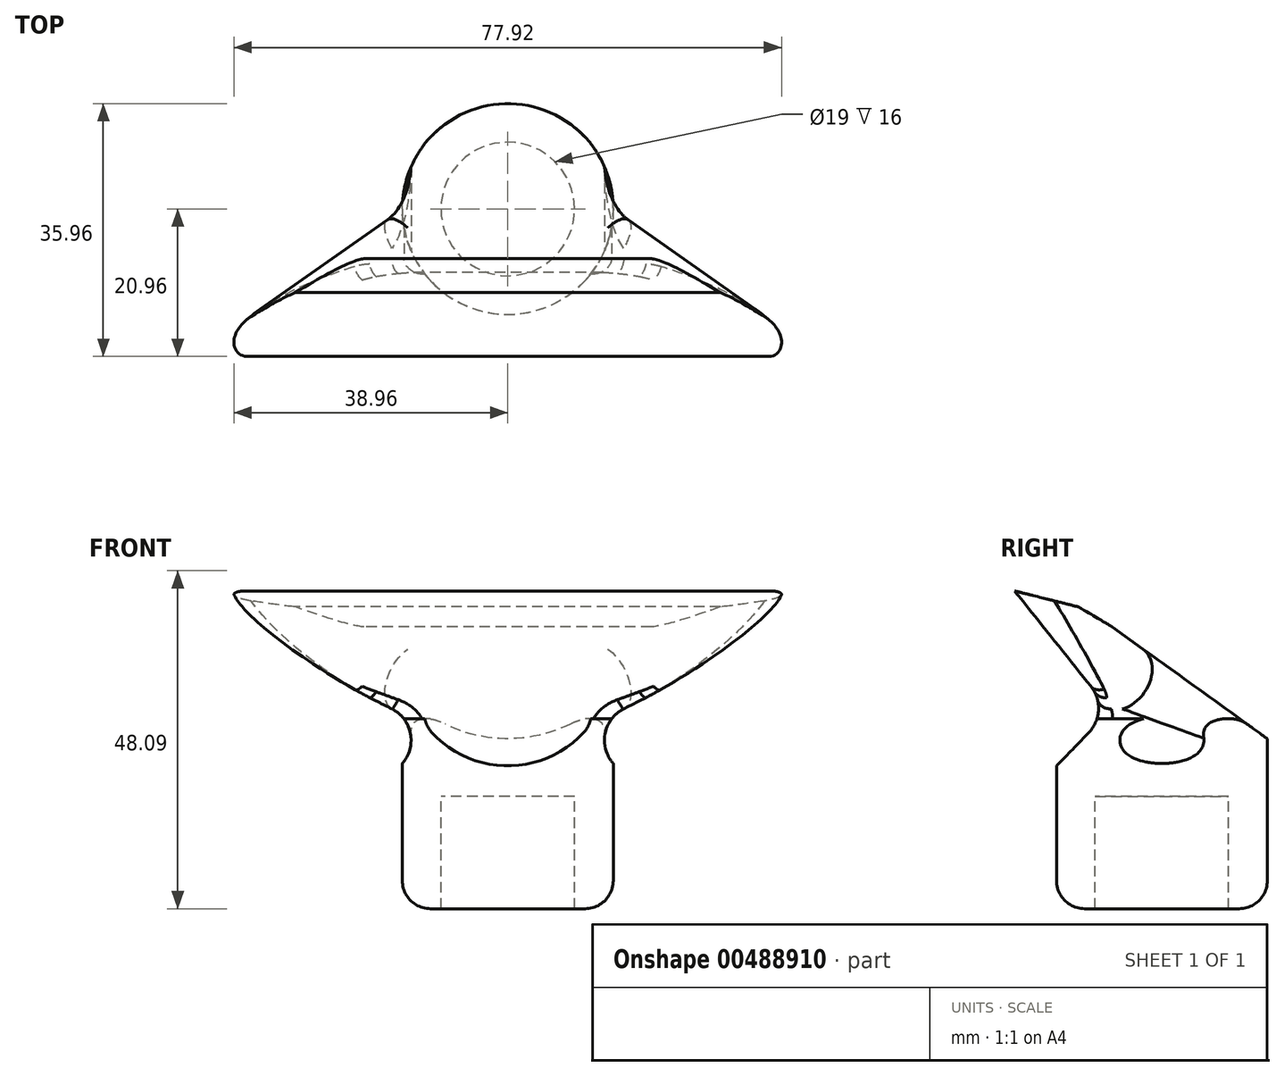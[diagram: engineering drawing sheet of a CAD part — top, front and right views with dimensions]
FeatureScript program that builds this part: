
annotation { "Feature Type Name" : "Feature", "Feature Type Description" : "" }
export const myFeature = defineFeature(function(context is Context, id is Id, definition is map)
    precondition{}
    {
        {
            var Q0;
            Q0=qCreatedBy(makeId("Top.planeOp"),FACE);
            var sketch = newSketch(context, id + "F0", { "sketchPlane" : qUnion([Q0])});
            skCircle(sketch, "E0", {"center": v(0, 0) * mm, "radius": 9.5 * mm});
            skCircle(sketch, "E1", {"center": v(0, 0) * mm, "radius": 15 * mm});
            skSolve(sketch);
        }
        {
            var Q0;
            Q0=makeQuery(id+"F0.imprint","IMPRINT",FACE,{"disambiguationData":[TD([[makeQuery(id+"F0.imprint","IMPRINT",EDGE,{"derivedFrom":sQuery(id+"F0.wireOp",EDGE,"E0")}),-1.0]])]});
            extrude(context, id + "F1", {"entities" : qUnion([Q0]), "oppositeDirection" : true, "depth" : 20 * mm, "offsetDistance" : 25 * mm});
        }
        {
            var Q0;
            Q0=makeQuery(id+"F1.opExtrude","CAP_EDGE",EDGE,{"disambiguationData":[OSD([sQuery(id+"F0.wireOp",EDGE,"E1")])],"isStart":false});
            fillet(context, id + "F2", {"entities" : qUnion([Q0]), "radius" : 4 * mm, "tangentPropagation" : true, "allowEdgeOverflow" : false});
        }
        {
            var Q0;
            Q0=makeQuery(id+"F0.imprint","IMPRINT",FACE,{"disambiguationData":[TD([[makeQuery(id+"F0.imprint","IMPRINT",EDGE,{"derivedFrom":sQuery(id+"F0.wireOp",EDGE,"E0")}),1.0]])]});
            extrude(context, id + "F3", {"entities" : qUnion([Q0]), "operationType" : NewBodyOperationType.ADD, "oppositeDirection" : true, "depth" : 4 * mm, "offsetDistance" : 25 * mm});
        }
        {
            var Q0;
            Q0=qCreatedBy(makeId("Right.planeOp"),FACE);
            var sketch = newSketch(context, id + "F4", { "sketchPlane" : qUnion([Q0])});
            skLineSegment(sketch, "E2", {"start": v(-7.08, 20.11) * mm, "end": v(15.3, 3.97) * mm});
            skLineSegment(sketch, "E3", {"start": v(15.3, 3.97) * mm, "end": v(15.3, 0) * mm});
            skLineSegment(sketch, "E4", {"start": v(15.3, 0) * mm, "end": v(-15.3, 0) * mm});
            skLineSegment(sketch, "E5", {"start": v(-15.3, 0) * mm, "end": v(-10.42, 5.05) * mm});
            skLineSegment(sketch, "E6", {"start": v(-10.11, 11.65) * mm, "end": v(-20.96, 25.21) * mm});
            skLineSegment(sketch, "E7", {"start": v(-20.96, 25.21) * mm, "end": v(-11.9, 22.95) * mm});
            skLineSegment(sketch, "E8", {"start": v(-11.9, 22.95) * mm, "end": v(-7.08, 20.11) * mm});
            skPoint(sketch, "E9.visualSharp", {"position": v(-7.37, 8.21) * mm});
            skArc(sketch, "E9.filletArc", {"start": v(-10.42, 5.05) * mm, "mid": v(-9.02, 8.3) * mm, "end": v(-10.11, 11.65) * mm});
            skSolve(sketch);
        }
        {
            var Q0;
            Q0=makeQuery(id+"F4.imprint","IMPRINT",FACE,{"disambiguationData":[TD([[makeQuery(id+"F4.imprint","IMPRINT",EDGE,{"derivedFrom":sQuery(id+"F4.wireOp",EDGE,"E2")}),-1.0]])]});
            extrude(context, id + "F5", {"entities" : qUnion([Q0]), "operationType" : NewBodyOperationType.ADD, "depth" : 40 * mm, "offsetDistance" : 25 * mm, "hasSecondDirection" : true, "secondDirectionOppositeDirection" : true, "secondDirectionDepth" : 40 * mm});
        }
        {
            var Q0;
            Q0=qCreatedBy(makeId("Front.planeOp"),FACE);
            var sketch = newSketch(context, id + "F6", { "sketchPlane" : qUnion([Q0])});
            skLineSegment(sketch, "E10", {"start": v(19.55, -5.1) * mm, "end": v(11.05, 5.67) * mm});
            skLineSegment(sketch, "E11", {"start": v(11.05, 5.67) * mm, "end": v(46.17, 23.51) * mm});
            skLineSegment(sketch, "E12", {"start": v(46.17, 23.51) * mm, "end": v(59.38, -2.48) * mm});
            skLineSegment(sketch, "E13", {"start": v(59.38, -2.48) * mm, "end": v(19.55, -5.1) * mm});
            skSolve(sketch);
        }
        {
            var Q0;
            Q0=makeQuery(id+"F6.imprint","IMPRINT",FACE,{"disambiguationData":[TD([[makeQuery(id+"F6.imprint","IMPRINT",EDGE,{"derivedFrom":sQuery(id+"F6.wireOp",EDGE,"E10")}),-1.0]])]});
            extrude(context, id + "F7", {"entities" : qUnion([Q0]), "depth" : 25 * mm, "offsetDistance" : 25 * mm, "hasSecondDirection" : true, "secondDirectionOppositeDirection" : true, "secondDirectionDepth" : 25 * mm});
        }
        {
            var Q0;
            Q0=makeQuery(id+"F7.opExtrude","SWEPT_BODY",BODY,{"disambiguationData":[OSD([sQuery(id+"F6.wireOp",EDGE,"E10"),sQuery(id+"F6.wireOp",EDGE,"E11"),sQuery(id+"F6.wireOp",EDGE,"E12"),sQuery(id+"F6.wireOp",EDGE,"E13")])]});
            var Q1;
            Q1=qCreatedBy(makeId("Right.planeOp"),FACE);
            mirror(context, id + "F8", {"entities" : qUnion([Q0]), "mirrorPlane" : qUnion([Q1])});
        }
        {
            var Q0;
            Q0=makeQuery(id+"F7.opExtrude","SWEPT_BODY",BODY,{"disambiguationData":[OSD([sQuery(id+"F6.wireOp",EDGE,"E10"),sQuery(id+"F6.wireOp",EDGE,"E11"),sQuery(id+"F6.wireOp",EDGE,"E12"),sQuery(id+"F6.wireOp",EDGE,"E13")])]});
            var Q1;
            Q1=makeQuery(id+"F8.opPattern","COPY",BODY,{"derivedFrom":makeQuery(id+"F7.opExtrude","SWEPT_BODY",BODY,{"disambiguationData":[OSD([sQuery(id+"F6.wireOp",EDGE,"E10"),sQuery(id+"F6.wireOp",EDGE,"E11"),sQuery(id+"F6.wireOp",EDGE,"E12"),sQuery(id+"F6.wireOp",EDGE,"E13")])]}),"instanceName":"1"});
            var Q2;
            Q2=makeQuery(id+"F1.opExtrude","SWEPT_BODY",BODY,{"disambiguationData":[OSD([sQuery(id+"F0.wireOp",EDGE,"E0"),sQuery(id+"F0.wireOp",EDGE,"E1")])]});
            booleanBodies(context, id + "F9", {"operationType" : BooleanOperationType.SUBTRACTION, "tools" : qUnion([Q0, Q1]), "targets" : qUnion([Q2])});
        }
        {
            var Q0;
            Q0=makeQuery(id+"F9.opBoolean","COPY",EDGE,{"derivedFrom":makeQuery(id+"F8.opPattern","COPY",EDGE,{"derivedFrom":makeQuery(id+"F7.opExtrude","SWEPT_EDGE",EDGE,{"disambiguationData":[OSD([sQuery(id+"F6.wireOp",EDGE,"E10"),sQuery(id+"F6.wireOp",EDGE,"E11")])]}),"instanceName":"1"})});
            var Q1;
            Q1=makeQuery(id+"F9.opBoolean","COPY",EDGE,{"derivedFrom":makeQuery(id+"F7.opExtrude","SWEPT_EDGE",EDGE,{"disambiguationData":[OSD([sQuery(id+"F6.wireOp",EDGE,"E10"),sQuery(id+"F6.wireOp",EDGE,"E11")])]})});
            fillet(context, id + "F10", {"entities" : qUnion([Q0, Q1]), "radius" : 5 * mm, "tangentPropagation" : true, "allowEdgeOverflow" : false});
        }
        {
            var Q0;
            Q0=qCreatedBy(makeId("Top.planeOp"),FACE);
            var sketch = newSketch(context, id + "F11", { "sketchPlane" : qUnion([Q0])});
            skCircle(sketch, "E14", {"center": v(0, 0) * mm, "radius": 15 * mm});
            skCircle(sketch, "E15", {"center": v(0, 0) * mm, "radius": 22.47 * mm});
            skSolve(sketch);
        }
        {
            var Q0;
            Q0=makeQuery(id+"F11.imprint","IMPRINT",FACE,{"disambiguationData":[TD([[makeQuery(id+"F11.imprint","IMPRINT",EDGE,{"derivedFrom":sQuery(id+"F11.wireOp",EDGE,"E14")}),-1.0]])]});
            extrude(context, id + "F12", {"entities" : qUnion([Q0]), "operationType" : NewBodyOperationType.REMOVE, "depth" : 7 * mm, "offsetDistance" : 25 * mm});
        }
        {
            var Q0;
            Q0=makeQuery(id+"F9.opBoolean","INTERSECT",EDGE,{"derivedFrom":[makeQuery(id+"F5.opExtrude","SWEPT_FACE",FACE,{"disambiguationData":[OSD([sQuery(id+"F4.wireOp",EDGE,"E2")])]}),makeQuery(id+"F8.opPattern","COPY",FACE,{"derivedFrom":makeQuery(id+"F7.opExtrude","SWEPT_FACE",FACE,{"disambiguationData":[OSD([sQuery(id+"F6.wireOp",EDGE,"E11")])]}),"instanceName":"1"})]});
            var Q1;
            Q1=makeQuery(id+"F9.opBoolean","INTERSECT",EDGE,{"derivedFrom":[makeQuery(id+"F5.opExtrude","SWEPT_FACE",FACE,{"disambiguationData":[OSD([sQuery(id+"F4.wireOp",EDGE,"E2")])]}),makeQuery(id+"F7.opExtrude","SWEPT_FACE",FACE,{"disambiguationData":[OSD([sQuery(id+"F6.wireOp",EDGE,"E11")])]})]});
            fillet(context, id + "F13", {"entities" : qUnion([Q0, Q1]), "radius" : 5 * mm, "tangentPropagation" : true, "allowEdgeOverflow" : false});
        }
        {
            var Q0;
            Q0=makeQuery(id+"F13.opFillet","BLEND_EDGE",EDGE,{"blendedFrom":[makeQuery(id+"F9.opBoolean","INTERSECT",EDGE,{"derivedFrom":[makeQuery(id+"F5.opExtrude","SWEPT_FACE",FACE,{"disambiguationData":[OSD([sQuery(id+"F4.wireOp",EDGE,"E2")])]}),makeQuery(id+"F7.opExtrude","SWEPT_FACE",FACE,{"disambiguationData":[OSD([sQuery(id+"F6.wireOp",EDGE,"E11")])]})]}),makeQuery(id+"F5.opExtrude","SWEPT_FACE",FACE,{"disambiguationData":[OSD([sQuery(id+"F4.wireOp",EDGE,"E6")])]})],"blendedInto":[makeQuery(id+"F5.opExtrude","SWEPT_FACE",FACE,{"disambiguationData":[OSD([sQuery(id+"F4.wireOp",EDGE,"E6")])]})]});
            fillet(context, id + "F14", {"entities" : qUnion([Q0]), "radius" : 2 * mm, "tangentPropagation" : true, "allowEdgeOverflow" : false});
        }
        {
            var Q0;
            Q0=makeQuery(id+"F13.opFillet","BLEND_EDGE",EDGE,{"blendedFrom":[makeQuery(id+"F9.opBoolean","INTERSECT",EDGE,{"derivedFrom":[makeQuery(id+"F5.opExtrude","SWEPT_FACE",FACE,{"disambiguationData":[OSD([sQuery(id+"F4.wireOp",EDGE,"E2")])]}),makeQuery(id+"F8.opPattern","COPY",FACE,{"derivedFrom":makeQuery(id+"F7.opExtrude","SWEPT_FACE",FACE,{"disambiguationData":[OSD([sQuery(id+"F6.wireOp",EDGE,"E11")])]}),"instanceName":"1"})]}),makeQuery(id+"F5.opExtrude","SWEPT_FACE",FACE,{"disambiguationData":[OSD([sQuery(id+"F4.wireOp",EDGE,"E6")])]})],"blendedInto":[makeQuery(id+"F5.opExtrude","SWEPT_FACE",FACE,{"disambiguationData":[OSD([sQuery(id+"F4.wireOp",EDGE,"E6")])]})]});
            fillet(context, id + "F15", {"entities" : qUnion([Q0]), "radius" : 2 * mm, "tangentPropagation" : true, "allowEdgeOverflow" : false});
        }
    });
